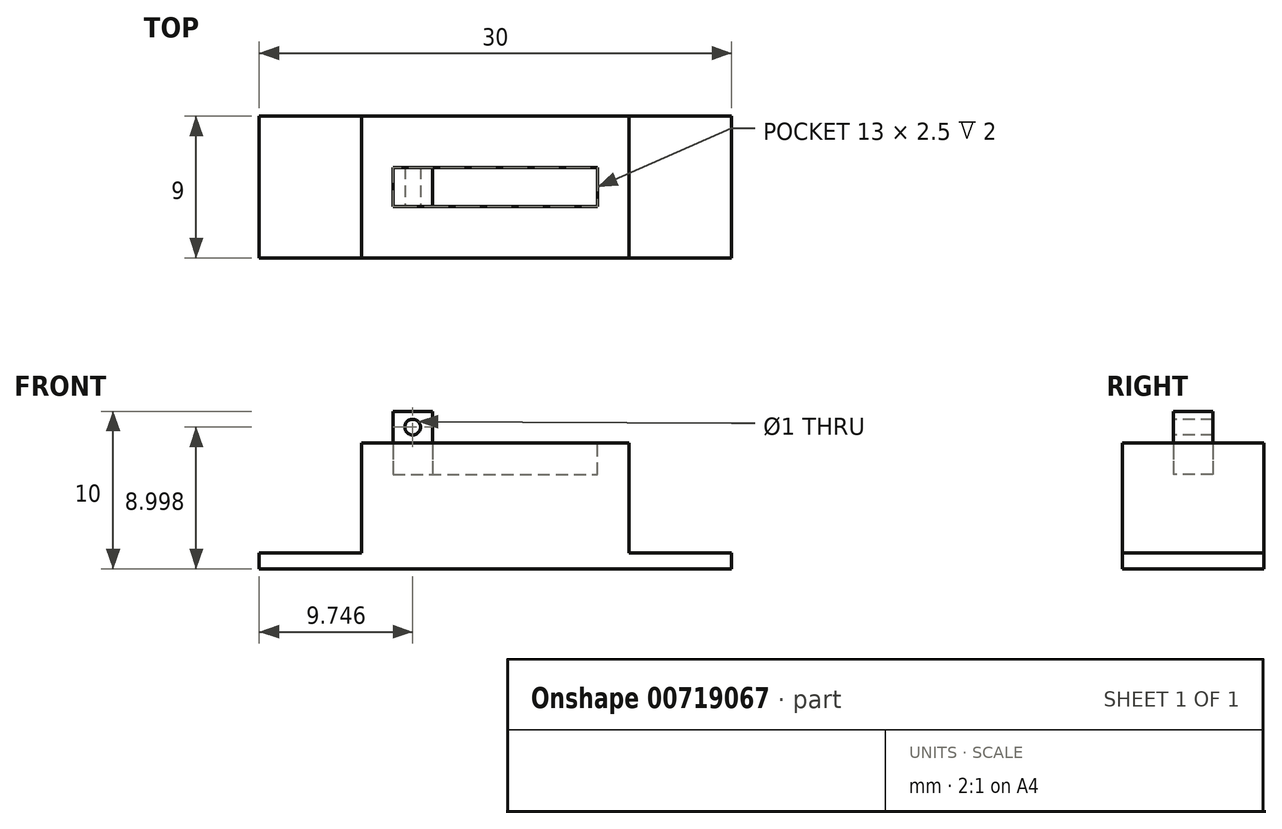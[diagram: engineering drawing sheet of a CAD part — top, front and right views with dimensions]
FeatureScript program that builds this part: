
annotation { "Feature Type Name" : "Feature", "Feature Type Description" : "" }
export const myFeature = defineFeature(function(context is Context, id is Id, definition is map)
    precondition{}
    {
        {
            var Q0;
            Q0=qCreatedBy(makeId("Front.planeOp"),FACE);
            var sketch = newSketch(context, id + "F0", { "sketchPlane" : qUnion([Q0])});
            skLineSegment(sketch, "E0.bottom", {"start": v(-7.7, 3.1) * mm, "end": v(9.3, 3.1) * mm});
            skLineSegment(sketch, "E0.left", {"start": v(-7.7, 3.1) * mm, "end": v(-7.7, -3.9) * mm});
            skLineSegment(sketch, "E0.right", {"start": v(9.3, 3.1) * mm, "end": v(9.3, -3.9) * mm});
            skLineSegment(sketch, "E1.bottom", {"start": v(-14.2, -3.9) * mm, "end": v(-7.7, -3.9) * mm});
            skLineSegment(sketch, "E1.top", {"start": v(-14.2, -4.9) * mm, "end": v(15.8, -4.9) * mm});
            skLineSegment(sketch, "E1.left", {"start": v(-14.2, -3.9) * mm, "end": v(-14.2, -4.9) * mm});
            skLineSegment(sketch, "E1.right", {"start": v(15.8, -3.9) * mm, "end": v(15.8, -4.9) * mm});
            skLineSegment(sketch, "E2.trimOffspring", {"start": v(9.3, -3.9) * mm, "end": v(15.8, -3.9) * mm});
            skSolve(sketch);
        }
        {
            var Q0;
            Q0=makeQuery(id+"F0.imprint","IMPRINT",FACE,{"disambiguationData":[TD([[makeQuery(id+"F0.imprint","IMPRINT",EDGE,{"derivedFrom":sQuery(id+"F0.wireOp",EDGE,"E0.bottom")}),-1.0]])]});
            extrude(context, id + "F1", {"entities" : qUnion([Q0]), "endBound" : BoundingType.SYMMETRIC, "depth" : 9 * mm, "offsetDistance" : 25 * mm});
        }
        {
            var Q0;
            Q0=makeQuery(id+"F1.opExtrude","SWEPT_FACE",FACE,{"disambiguationData":[OSD([sQuery(id+"F0.wireOp",EDGE,"E0.bottom")])]});
            var sketch = newSketch(context, id + "F2", { "sketchPlane" : qUnion([Q0])});
            skLineSegment(sketch, "E3.bottom", {"start": v(-5.7, 1.25) * mm, "end": v(7.3, 1.25) * mm});
            skLineSegment(sketch, "E3.top", {"start": v(-5.7, -1.25) * mm, "end": v(7.3, -1.25) * mm});
            skLineSegment(sketch, "E3.left", {"start": v(-5.7, 1.25) * mm, "end": v(-5.7, -1.25) * mm});
            skLineSegment(sketch, "E3.right", {"start": v(7.3, 1.25) * mm, "end": v(7.3, -1.25) * mm});
            skSolve(sketch);
        }
        {
            var Q0;
            Q0=makeQuery(id+"F2.imprint","IMPRINT",FACE,{"disambiguationData":[TD([[makeQuery(id+"F2.imprint","IMPRINT",EDGE,{"derivedFrom":sQuery(id+"F2.wireOp",EDGE,"E3.bottom")}),-1.0]])]});
            extrude(context, id + "F3", {"entities" : qUnion([Q0]), "operationType" : NewBodyOperationType.REMOVE, "oppositeDirection" : true, "depth" : 2 * mm, "offsetDistance" : 25 * mm});
        }
        {
            var Q0;
            Q0=makeQuery(id+"F3.boolean.opBoolean","COPY",FACE,{"derivedFrom":makeQuery(id+"F3.opExtrude","CAP_FACE",FACE,{"disambiguationData":[OSD([sQuery(id+"F2.wireOp",EDGE,"E3.bottom"),sQuery(id+"F2.wireOp",EDGE,"E3.top"),sQuery(id+"F2.wireOp",EDGE,"E3.left"),sQuery(id+"F2.wireOp",EDGE,"E3.right")])],"isStart":false})});
            var sketch = newSketch(context, id + "F4", { "sketchPlane" : qUnion([Q0])});
            skLineSegment(sketch, "E4.bottom", {"start": v(-5.7, 1.25) * mm, "end": v(-3.2, 1.25) * mm});
            skLineSegment(sketch, "E4.top", {"start": v(-5.7, -1.25) * mm, "end": v(-3.2, -1.25) * mm});
            skLineSegment(sketch, "E4.left", {"start": v(-5.7, 1.25) * mm, "end": v(-5.7, -1.25) * mm});
            skLineSegment(sketch, "E4.right", {"start": v(-3.2, 1.25) * mm, "end": v(-3.2, -1.25) * mm});
            skSolve(sketch);
        }
        {
            var Q0;
            Q0=makeQuery(id+"F4.imprint","IMPRINT",FACE,{"disambiguationData":[TD([[makeQuery(id+"F4.imprint","IMPRINT",EDGE,{"derivedFrom":sQuery(id+"F4.wireOp",EDGE,"E4.bottom")}),-1.0]])]});
            extrude(context, id + "F5", {"entities" : qUnion([Q0]), "depth" : 4 * mm, "offsetDistance" : 25 * mm});
        }
        {
            var Q0;
            Q0=makeQuery(id+"F5.opExtrude","SWEPT_FACE",FACE,{"disambiguationData":[OSD([sQuery(id+"F4.wireOp",EDGE,"E4.top")])]});
            var sketch = newSketch(context, id + "F6", { "sketchPlane" : qUnion([Q0])});
            skCircle(sketch, "E5", {"center": v(-4.45, 4.1) * mm, "radius": 0.5 * mm});
            skSolve(sketch);
        }
        {
            var Q0;
            Q0=makeQuery(id+"F6.imprint","IMPRINT",FACE,{"disambiguationData":[TD([[makeQuery(id+"F6.imprint","IMPRINT",EDGE,{"derivedFrom":sQuery(id+"F6.wireOp",EDGE,"E5")}),1.0]])]});
            extrude(context, id + "F7", {"entities" : qUnion([Q0]), "operationType" : NewBodyOperationType.REMOVE, "endBound" : BoundingType.THROUGH_ALL, "oppositeDirection" : true, "depth" : 25 * mm, "offsetDistance" : 25 * mm});
        }
    });
